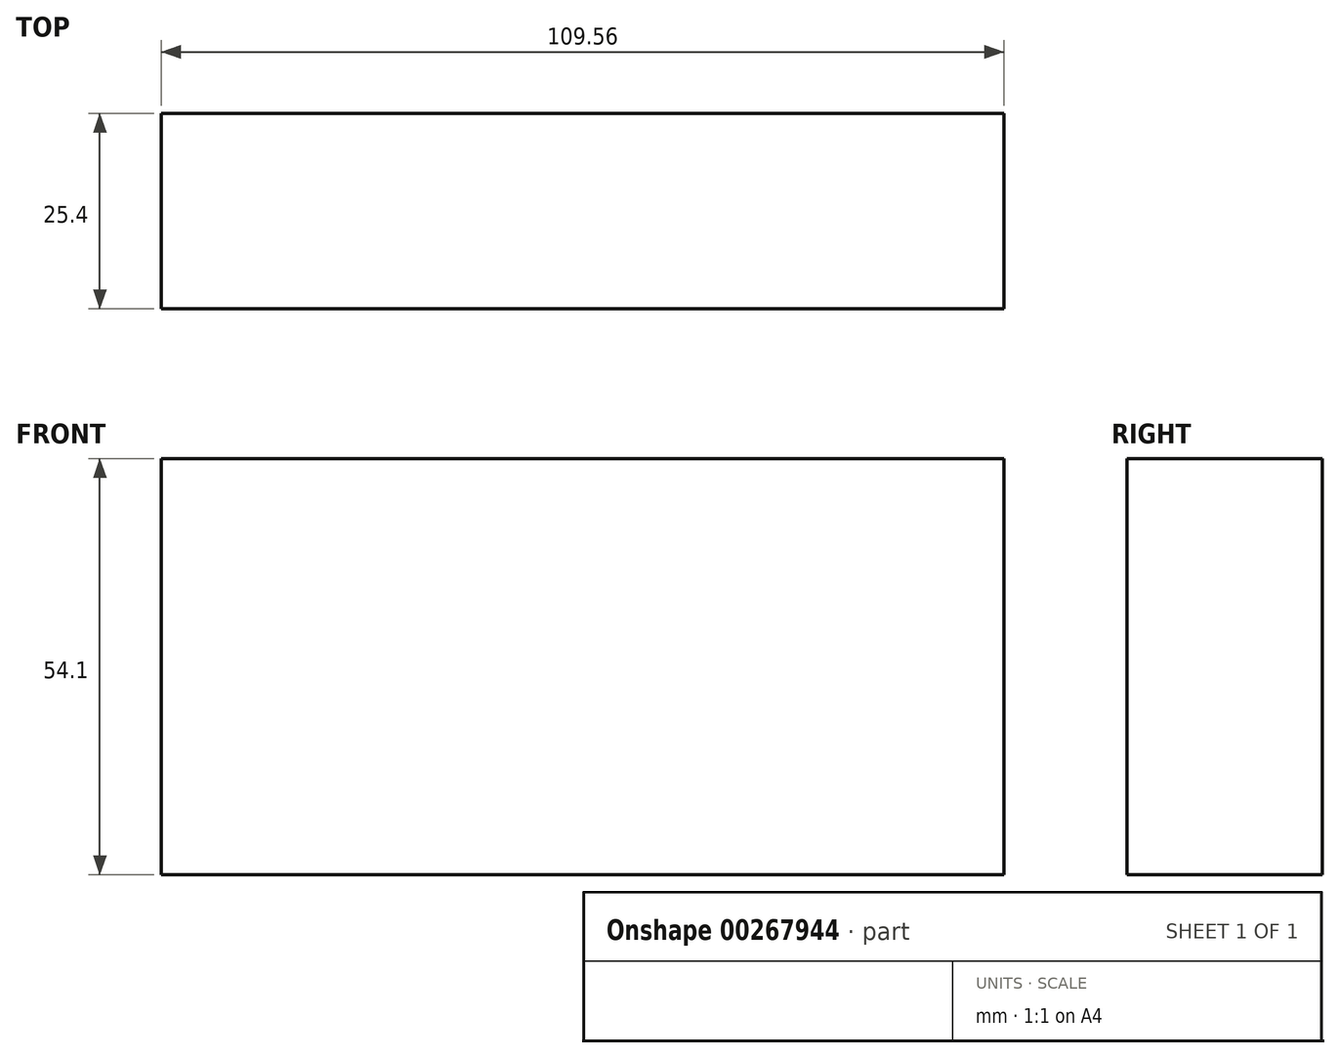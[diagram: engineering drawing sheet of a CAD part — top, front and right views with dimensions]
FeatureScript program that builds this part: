
annotation { "Feature Type Name" : "Feature", "Feature Type Description" : "" }
export const myFeature = defineFeature(function(context is Context, id is Id, definition is map)
    precondition{}
    {
        {
            var Q0;
            Q0=qCreatedBy(makeId("Front.planeOp"),FACE);
            var sketch = newSketch(context, id + "F0", { "sketchPlane" : qUnion([Q0])});
            skLineSegment(sketch, "E0.bottom", {"start": v(54.78, 27.05) * mm, "end": v(-54.78, 27.05) * mm});
            skLineSegment(sketch, "E0.top", {"start": v(54.78, -27.05) * mm, "end": v(-54.78, -27.05) * mm});
            skLineSegment(sketch, "E0.left", {"start": v(54.78, 27.05) * mm, "end": v(54.78, -27.05) * mm});
            skLineSegment(sketch, "E0.right", {"start": v(-54.78, 27.05) * mm, "end": v(-54.78, -27.05) * mm});
            skPoint(sketch, "E0.middle", {"position": v(0, 0) * mm});
            skLineSegment(sketch, "E1", {"start": v(54.78, 27.05) * mm, "end": v(54.78, 58.89) * mm});
            skArc(sketch, "E2", {"start": v(54.78, 58.89) * mm, "mid": v(78.24, 81.83) * mm, "end": v(100.66, 57.86) * mm});
            skSolve(sketch);
        }
        {
            var Q0;
            Q0=makeQuery(id+"F0.imprint","IMPRINT",FACE,{"disambiguationData":[TD([[makeQuery(id+"F0.imprint","IMPRINT",EDGE,{"derivedFrom":sQuery(id+"F0.wireOp",EDGE,"E0.bottom")}),1.0]])]});
            extrude(context, id + "F1", {"entities" : qUnion([Q0]), "depth" : 25.4 * mm});
        }
    });
